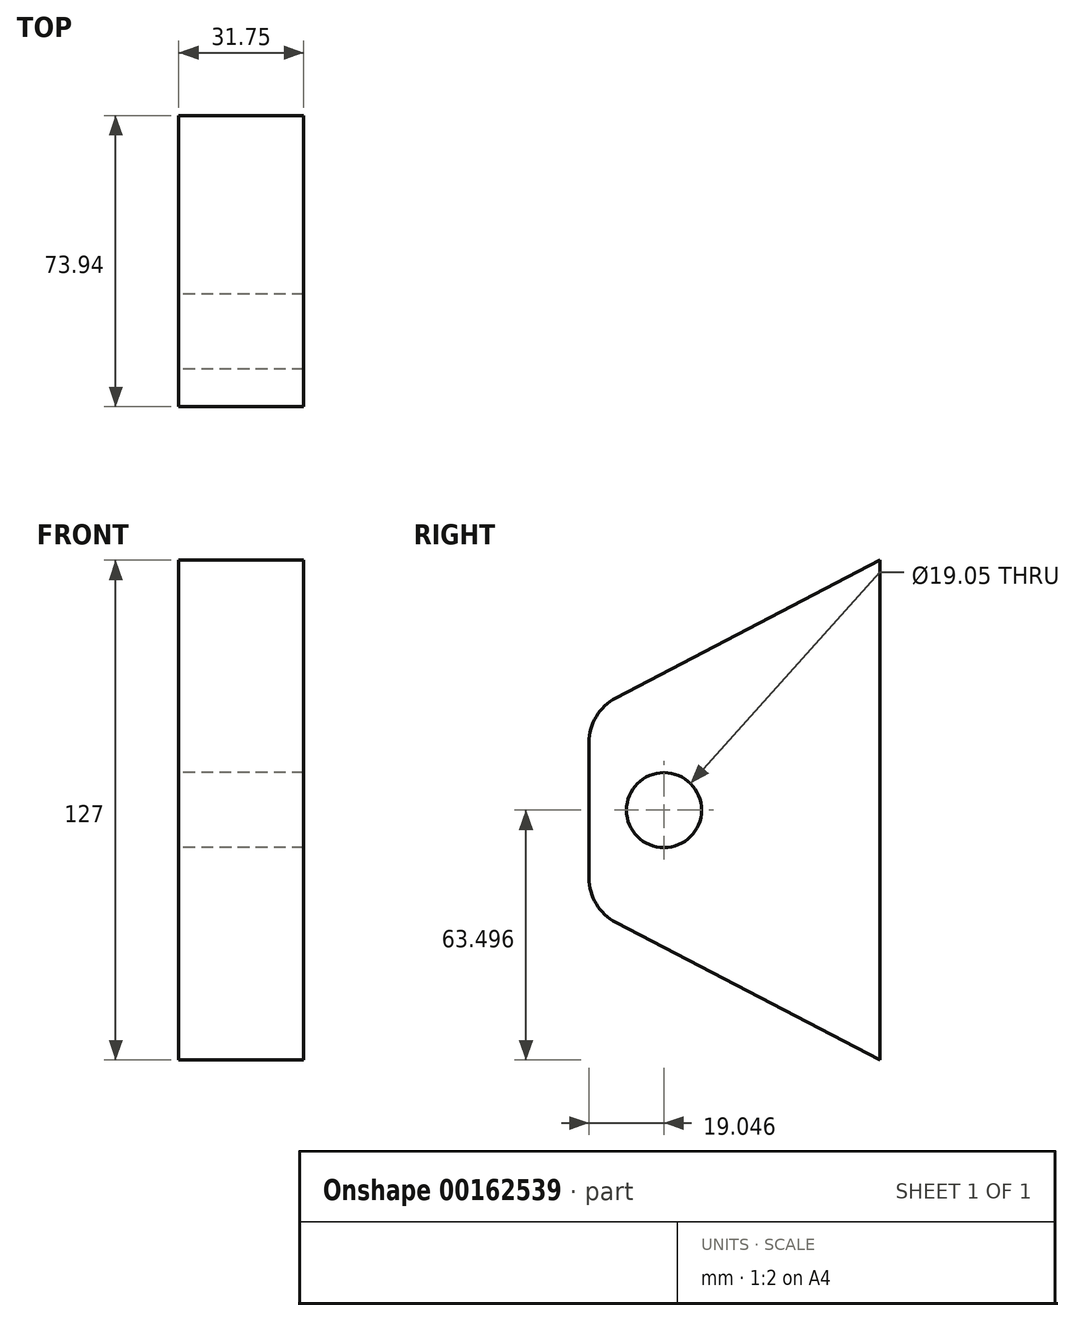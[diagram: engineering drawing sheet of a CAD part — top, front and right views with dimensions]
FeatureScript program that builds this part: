
annotation { "Feature Type Name" : "Feature", "Feature Type Description" : "" }
export const myFeature = defineFeature(function(context is Context, id is Id, definition is map)
    precondition{}
    {
        {
            var Q0;
            Q0=qCreatedBy(makeId("Right.planeOp"),FACE);
            var sketch = newSketch(context, id + "F0", { "sketchPlane" : qUnion([Q0])});
            skLineSegment(sketch, "E0.left", {"start": v(36.97, 72.7) * mm, "end": v(36.97, -54.3) * mm});
            skLineSegment(sketch, "E0.right", {"start": v(-36.97, 26.46) * mm, "end": v(-36.97, -8.06) * mm});
            skPoint(sketch, "E0.middle", {"position": v(0, 0) * mm});
            skPoint(sketch, "E1.visualSharp", {"position": v(-36.97, 54.3) * mm});
            skPoint(sketch, "E2.visualSharp", {"position": v(-36.97, -72.7) * mm});
            skLineSegment(sketch, "E3", {"start": v(-30.14, 37.72) * mm, "end": v(36.97, 72.7) * mm});
            skLineSegment(sketch, "E4", {"start": v(-30.14, -19.33) * mm, "end": v(36.97, -54.3) * mm});
            skPoint(sketch, "E5.visualSharp", {"position": v(-36.97, 34.16) * mm});
            skArc(sketch, "E5.filletArc", {"start": v(-30.14, 37.72) * mm, "mid": v(-35.13, 33.04) * mm, "end": v(-36.97, 26.46) * mm});
            skPoint(sketch, "E6.visualSharp", {"position": v(-36.97, -15.77) * mm});
            skArc(sketch, "E6.filletArc", {"start": v(-36.97, -8.06) * mm, "mid": v(-35.13, -14.65) * mm, "end": v(-30.14, -19.33) * mm});
            skLineSegment(sketch, "E7", {"start": v(-36.97, 9.2) * mm, "end": v(36.97, 9.2) * mm});
            skCircle(sketch, "E8", {"center": v(-17.92, 9.2) * mm, "radius": 9.53 * mm});
            skSolve(sketch);
        }
        {
            var Q0;
            Q0=qSketchRegion(id+"F0",true);
            extrude(context, id + "F1", {"entities" : qUnion([Q0]), "depth" : 31.75 * mm});
        }
    });
